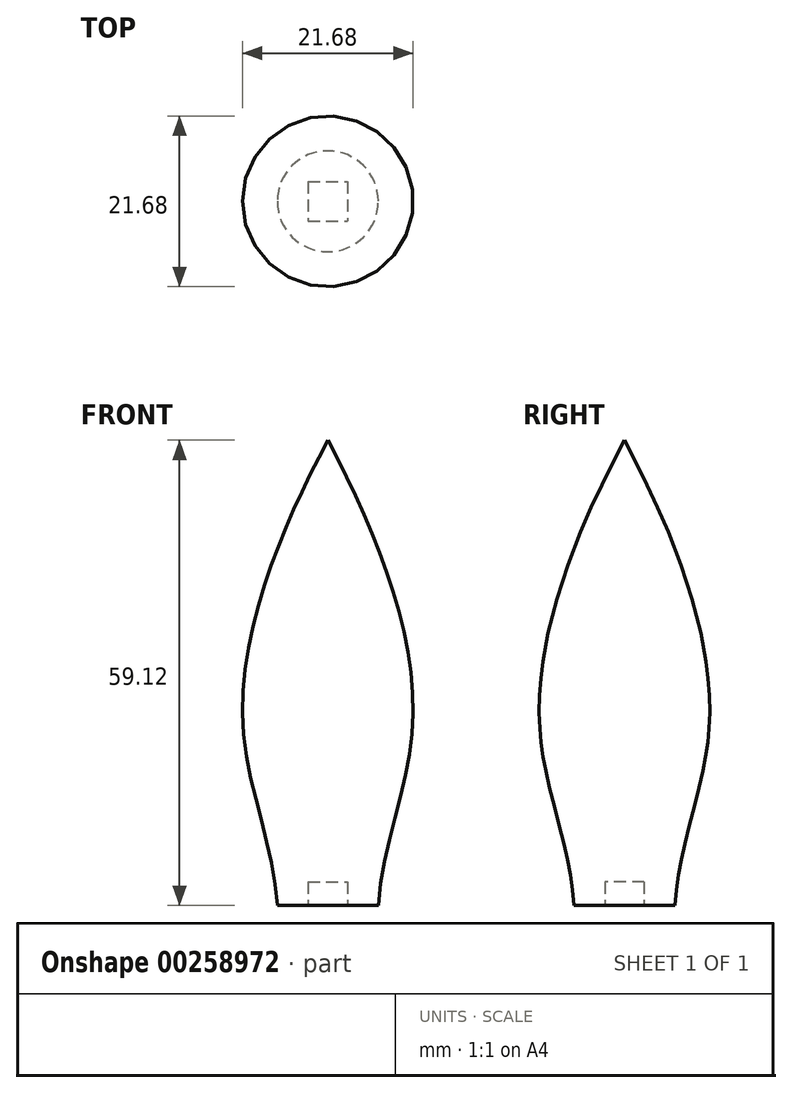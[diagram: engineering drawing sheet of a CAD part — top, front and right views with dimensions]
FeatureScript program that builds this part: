
annotation { "Feature Type Name" : "Feature", "Feature Type Description" : "" }
export const myFeature = defineFeature(function(context is Context, id is Id, definition is map)
    precondition{}
    {
        {
            var Q0;
            Q0=qCreatedBy(makeId("Front.planeOp"),FACE);
            var sketch = newSketch(context, id + "F0", { "sketchPlane" : qUnion([Q0])});
            skFitSpline(sketch, "E0", {"points": [v(0, 59.12) * mm, v(-7.36, 42.74) * mm, v(-10.68, 21.6) * mm, v(-6.41, 0) * mm], "startDerivative": vector(-26.28, -49.87) * mm, "endDerivative": vector(3.4, -62.42) * mm});
            skLineSegment(sketch, "E1", {"start": v(-6.41, 0) * mm, "end": v(0, 0) * mm});
            skLineSegment(sketch, "E2", {"start": v(0, 0) * mm, "end": v(0, 59.12) * mm});
            skSolve(sketch);
        }
        {
            var Q0;
            Q0=qCreatedBy(makeId("Front.planeOp"),FACE);
            var sketch = newSketch(context, id + "F1", { "sketchPlane" : qUnion([Q0])});
            skLineSegment(sketch, "E3", {"start": v(0, 72.41) * mm, "end": v(0, -31.1) * mm});
            skSolve(sketch);
        }
        {
            var Q0;
            Q0=makeQuery(id+"F0.imprint","IMPRINT",FACE,{"disambiguationData":[TD([[makeQuery(id+"F0.imprint","IMPRINT",EDGE,{"derivedFrom":sQuery(id+"F0.wireOp",EDGE,"E0")}),1.0]])]});
            var Q1;
            Q1=sQuery(id+"F0.wireOp",EDGE,"E0");
            var Q2;
            Q2=sQuery(id+"F0.wireOp",EDGE,"E1");
            var Q3;
            Q3=sQuery(id+"F0.wireOp",EDGE,"E2");
            var Q4;
            Q4=sQuery(id+"F1.wireOp",EDGE,"E3");
            revolve(context, id + "F2", {"entities" : qUnion([Q0]), "surfaceEntities" : qUnion([Q1, Q2, Q3]), "axis" : qUnion([Q4]), "revolveType" : RevolveType.FULL});
        }
        {
            var Q0;
            Q0=makeQuery(id+"F2.opRevolve","SWEPT_FACE",FACE,{"disambiguationData":[OSD([sQuery(id+"F0.wireOp",EDGE,"E1")])]});
            var sketch = newSketch(context, id + "F3", { "sketchPlane" : qUnion([Q0])});
            skLineSegment(sketch, "E4.bottom", {"start": v(-2.5, -2.5) * mm, "end": v(2.5, -2.5) * mm});
            skLineSegment(sketch, "E4.top", {"start": v(-2.5, 2.5) * mm, "end": v(2.5, 2.5) * mm});
            skLineSegment(sketch, "E4.left", {"start": v(-2.5, -2.5) * mm, "end": v(-2.5, 2.5) * mm});
            skLineSegment(sketch, "E4.right", {"start": v(2.5, -2.5) * mm, "end": v(2.5, 2.5) * mm});
            skLineSegment(sketch, "E5", {"start": v(-2.5, 0) * mm, "end": v(2.5, 0) * mm, "construction": true});
            skPoint(sketch, "E6", {"position": v(0, 0) * mm});
            skSolve(sketch);
        }
        {
            var Q0;
            Q0 = qSketchRegion(id + "F3", true);
            extrude(context, id + "F4", {"entities" : qUnion([Q0]), "operationType" : NewBodyOperationType.REMOVE, "oppositeDirection" : true, "depth" : 3 * mm});
        }
    });
